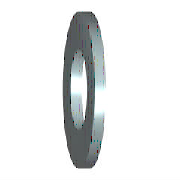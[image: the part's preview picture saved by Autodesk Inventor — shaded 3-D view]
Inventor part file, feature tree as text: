
AUTODESK INVENTOR PART (.ipt)
format: ipt  version: 2015 (Build 190159000, 159)  size: 105,984 bytes
history: native  units: mm (DEFAULTED — no unit token found)
features: other x1, plane x1, sketch x1
ambient origin geometry x7: Origin, YZ Plane, XY Plane, X Axis, Y Axis, Z Axis, Center Point
bodies: Solid1 (feature_tree), Body (feature_tree)
feature tree (3):
  other  "Work Axis1"
  plane  "Work Plane1"
  sketch  "Sketch"  dims[d0=10.5mm d1=30.0mm d2=2.5mm d3=0.0mm d4=0.0mm d5=0.0mm d6=0.0mm d7=0.0mm]
